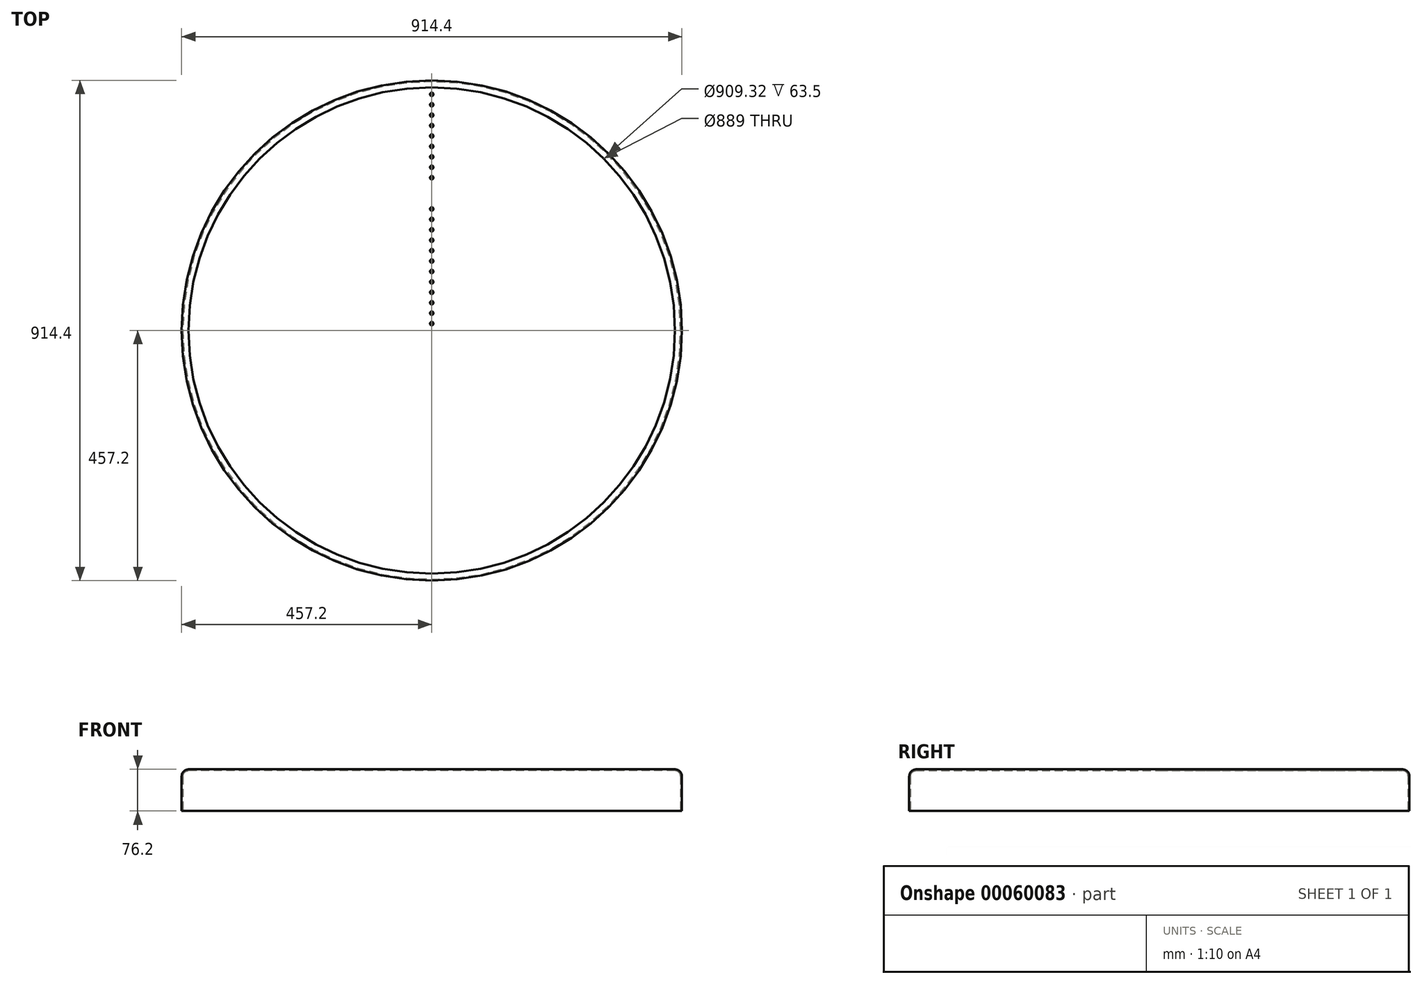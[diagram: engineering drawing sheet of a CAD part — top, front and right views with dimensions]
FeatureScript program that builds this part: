
annotation { "Feature Type Name" : "Feature", "Feature Type Description" : "" }
export const myFeature = defineFeature(function(context is Context, id is Id, definition is map)
    precondition{}
    {
        {
            var Q0;
            Q0=qCreatedBy(makeId("Top.planeOp"),FACE);
            var sketch = newSketch(context, id + "F0", { "sketchPlane" : qUnion([Q0])});
            skCircle(sketch, "E0", {"center": v(0, 0) * mm, "radius": 457.2 * mm});
            skSolve(sketch);
        }
        {
            var Q0;
            Q0=makeQuery(id+"F0.imprint","IMPRINT",FACE,{"disambiguationData":[TD([[makeQuery(id+"F0.imprint","IMPRINT",EDGE,{"derivedFrom":sQuery(id+"F0.wireOp",EDGE,"E0")}),1.0]])]});
            extrude(context, id + "F1", {"entities" : qUnion([Q0]), "depth" : 76.2 * mm});
        }
        {
            var Q0;
            Q0=makeQuery(id+"F1.opExtrude","CAP_EDGE",EDGE,{"disambiguationData":[OSD([sQuery(id+"F0.wireOp",EDGE,"E0")])],"isStart":false});
            fillet(context, id + "F2", {"entities" : qUnion([Q0]), "radius" : 12.7 * mm, "tangentPropagation" : true, "allowEdgeOverflow" : false});
        }
        {
            var Q0;
            Q0=makeQuery(id+"F1.opExtrude","CAP_FACE",FACE,{"disambiguationData":[OSD([sQuery(id+"F0.wireOp",EDGE,"E0")])],"isStart":true});
            shell(context, id + "F3", {"entities" : qUnion([Q0]), "thickness" : 2.54 * mm});
        }
        {
            var Q0;
            Q0=makeQuery(id+"F1.opExtrude","CAP_FACE",FACE,{"disambiguationData":[OSD([sQuery(id+"F0.wireOp",EDGE,"E0")])],"isStart":false});
            var sketch = newSketch(context, id + "F4", { "sketchPlane" : qUnion([Q0])});
            skCircle(sketch, "E1", {"center": v(0, 12.7) * mm, "radius": 3.18 * mm});
            skCircle(sketch, "E2.0.1.0", {"center": v(0, 31.75) * mm, "radius": 3.18 * mm});
            skCircle(sketch, "E2.0.2.0", {"center": v(0, 50.8) * mm, "radius": 3.18 * mm});
            skCircle(sketch, "E2.0.3.0", {"center": v(0, 69.85) * mm, "radius": 3.18 * mm});
            skCircle(sketch, "E2.0.4.0", {"center": v(0, 88.9) * mm, "radius": 3.18 * mm});
            skCircle(sketch, "E2.0.5.0", {"center": v(0, 107.95) * mm, "radius": 3.18 * mm});
            skCircle(sketch, "E2.0.6.0", {"center": v(0, 127) * mm, "radius": 3.18 * mm});
            skCircle(sketch, "E2.0.7.0", {"center": v(0, 146.05) * mm, "radius": 3.18 * mm});
            skCircle(sketch, "E2.0.8.0", {"center": v(0, 165.1) * mm, "radius": 3.18 * mm});
            skCircle(sketch, "E2.0.9.0", {"center": v(0, 184.15) * mm, "radius": 3.18 * mm});
            skCircle(sketch, "E2.0.10.0", {"center": v(0, 203.2) * mm, "radius": 3.18 * mm});
            skCircle(sketch, "E2.0.11.0", {"center": v(0, 222.25) * mm, "radius": 3.18 * mm});
            skCircle(sketch, "E2.0.12.0", {"center": v(0, 241.3) * mm, "radius": 3.18 * mm});
            skCircle(sketch, "E2.0.13.0", {"center": v(0, 260.35) * mm, "radius": 3.18 * mm});
            skCircle(sketch, "E2.0.14.0", {"center": v(0, 279.4) * mm, "radius": 3.18 * mm});
            skCircle(sketch, "E2.0.15.0", {"center": v(0, 298.45) * mm, "radius": 3.18 * mm});
            skCircle(sketch, "E2.0.16.0", {"center": v(0, 317.5) * mm, "radius": 3.18 * mm});
            skCircle(sketch, "E2.0.17.0", {"center": v(0, 336.55) * mm, "radius": 3.18 * mm});
            skCircle(sketch, "E2.0.18.0", {"center": v(0, 355.6) * mm, "radius": 3.18 * mm});
            skCircle(sketch, "E2.0.19.0", {"center": v(0, 374.65) * mm, "radius": 3.18 * mm});
            skLineSegment(sketch, "E2.direction1", {"start": v(0, 12.7) * mm, "end": v(25.4, 12.7) * mm, "construction": true});
            skLineSegment(sketch, "E2.direction2", {"start": v(0, 12.7) * mm, "end": v(0, 31.75) * mm, "construction": true});
            skCircle(sketch, "E3.0.0.20", {"center": v(0, 393.7) * mm, "radius": 3.18 * mm});
            skCircle(sketch, "E3.0.0.21", {"center": v(0, 412.75) * mm, "radius": 3.18 * mm});
            skCircle(sketch, "E3.0.0.22", {"center": v(0, 431.8) * mm, "radius": 3.18 * mm});
            skSolve(sketch);
        }
        {
            var Q0;
            Q0=makeQuery(id+"F4.imprint","IMPRINT",FACE,{"disambiguationData":[TD([[makeQuery(id+"F4.imprint","IMPRINT",EDGE,{"derivedFrom":sQuery(id+"F4.wireOp",EDGE,"E2.0.12.0")}),1.0]])]});
            var Q1;
            Q1=makeQuery(id+"F4.imprint","IMPRINT",FACE,{"disambiguationData":[TD([[makeQuery(id+"F4.imprint","IMPRINT",EDGE,{"derivedFrom":sQuery(id+"F4.wireOp",EDGE,"E2.0.13.0")}),1.0]])]});
            var Q2;
            Q2=makeQuery(id+"F4.imprint","IMPRINT",FACE,{"disambiguationData":[TD([[makeQuery(id+"F4.imprint","IMPRINT",EDGE,{"derivedFrom":sQuery(id+"F4.wireOp",EDGE,"E1")}),-1.0]])]});
            extrude(context, id + "F5", {"entities" : qUnion([Q0, Q1, Q2]), "operationType" : NewBodyOperationType.REMOVE, "oppositeDirection" : true, "depth" : 2.54 * mm});
        }
    });
